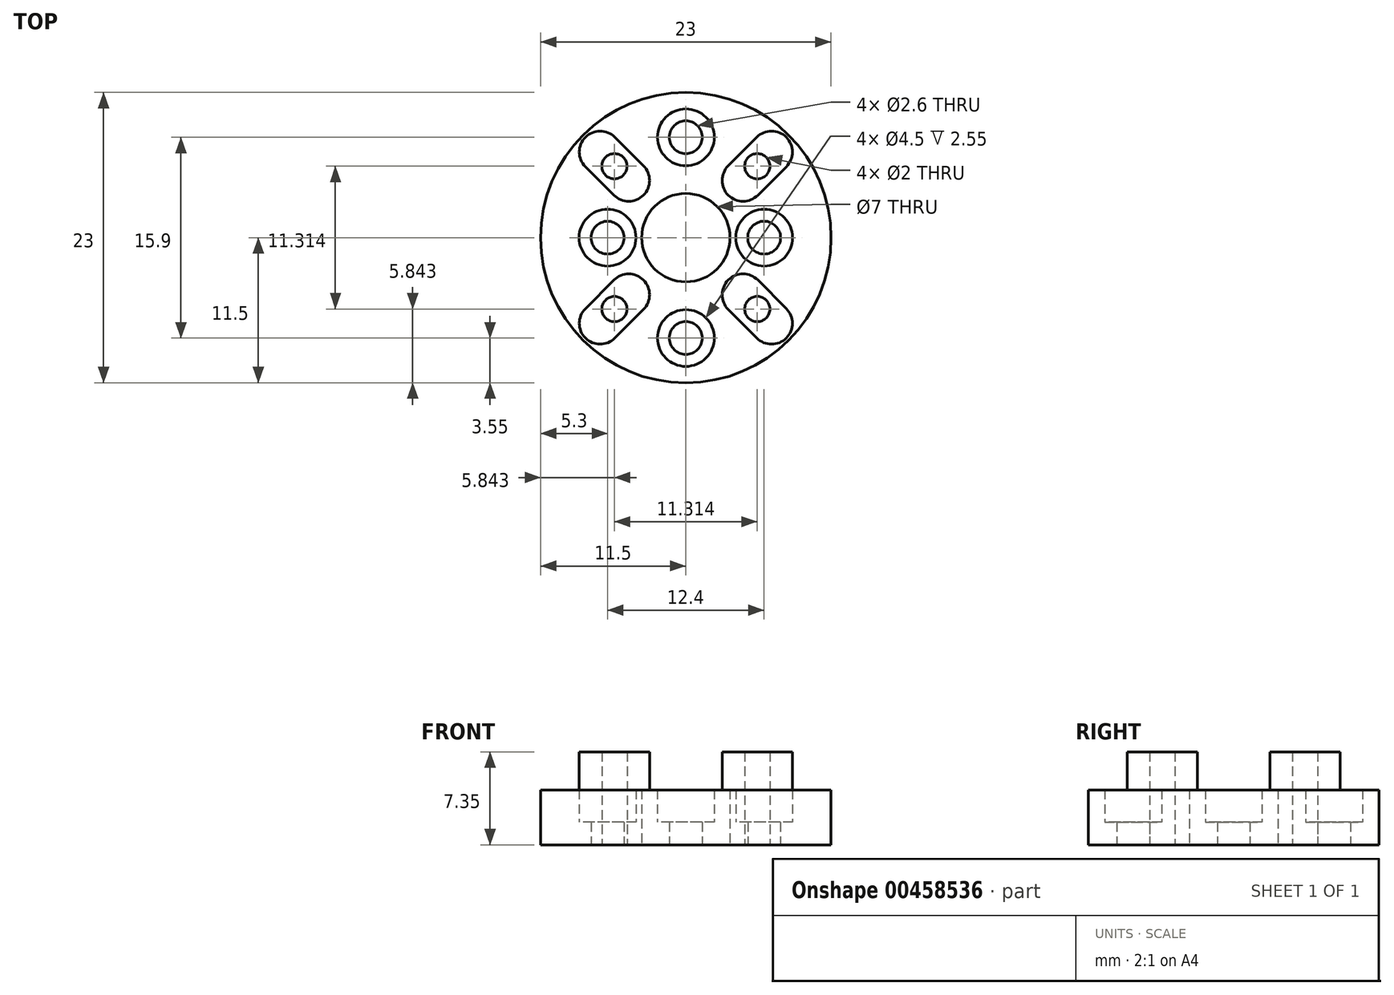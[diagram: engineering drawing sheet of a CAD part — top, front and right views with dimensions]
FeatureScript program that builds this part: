
annotation { "Feature Type Name" : "Feature", "Feature Type Description" : "" }
export const myFeature = defineFeature(function(context is Context, id is Id, definition is map)
    precondition{}
    {
        {
            var Q0;
            Q0=qCreatedBy(makeId("Top.planeOp"),FACE);
            var sketch = newSketch(context, id + "F0", { "sketchPlane" : qUnion([Q0])});
            skCircle(sketch, "E0", {"center": v(0, 0) * mm, "radius": 11.5 * mm});
            skCircle(sketch, "E1", {"center": v(0, 0) * mm, "radius": 3.5 * mm});
            skCircle(sketch, "E2", {"center": v(6.2, 0) * mm, "radius": 1.3 * mm});
            skCircle(sketch, "E3", {"center": v(-6.2, 0) * mm, "radius": 1.3 * mm});
            skCircle(sketch, "E4", {"center": v(0, 7.95) * mm, "radius": 1.3 * mm});
            skCircle(sketch, "E5", {"center": v(0, -7.95) * mm, "radius": 1.3 * mm});
            skSolve(sketch);
        }
        {
            var Q0;
            Q0=qSketchRegion(id+"F0",true);
            extrude(context, id + "F1", {"entities" : qUnion([Q0]), "depth" : 4.35 * mm});
        }
        {
            var Q0;
            Q0=qCreatedBy(makeId("Top.planeOp"),FACE);
            cPlane(context, id + "F2", {"entities" : qUnion([Q0]), "cplaneType" : CPlaneType.OFFSET, "offset" : 4.35 * mm, "width" : 150 * mm, "height" : 150 * mm});
        }
        {
            var Q0;
            Q0=qCreatedBy(id+"F2.planeOp",FACE);
            var sketch = newSketch(context, id + "F3", { "sketchPlane" : qUnion([Q0])});
            skLineSegment(sketch, "E6", {"start": v(0, 0) * mm, "end": v(4.53, -4.53) * mm, "construction": true});
            skLineSegment(sketch, "E7", {"start": v(0, 0) * mm, "end": v(4.53, 4.53) * mm, "construction": true});
            skLineSegment(sketch, "E8", {"start": v(4.53, -4.53) * mm, "end": v(6.79, -6.79) * mm});
            skArc(sketch, "E9.0.startCap", {"start": v(3.36, -5.7) * mm, "mid": v(3.36, -3.36) * mm, "end": v(5.7, -3.36) * mm});
            skArc(sketch, "E9.0.endCap", {"start": v(7.95, -5.62) * mm, "mid": v(7.95, -7.95) * mm, "end": v(5.62, -7.95) * mm});
            skLineSegment(sketch, "E9.0.left", {"start": v(5.7, -3.36) * mm, "end": v(7.95, -5.62) * mm});
            skLineSegment(sketch, "E9.0.right", {"start": v(3.36, -5.7) * mm, "end": v(5.62, -7.95) * mm});
            skLineSegment(sketch, "E10.MirrorCS", {"start": v(4.53, 4.53) * mm, "end": v(6.79, 6.79) * mm});
            skLineSegment(sketch, "E11.MirrorCS", {"start": v(-4.53, 4.53) * mm, "end": v(-6.79, 6.79) * mm});
            skLineSegment(sketch, "E12.MirrorCS", {"start": v(-4.53, -4.53) * mm, "end": v(-6.79, -6.79) * mm});
            skArc(sketch, "E13.0.startCap", {"start": v(5.7, 3.36) * mm, "mid": v(3.36, 3.36) * mm, "end": v(3.36, 5.7) * mm});
            skArc(sketch, "E13.0.endCap", {"start": v(5.62, 7.95) * mm, "mid": v(7.95, 7.95) * mm, "end": v(7.95, 5.62) * mm});
            skLineSegment(sketch, "E13.0.left", {"start": v(3.36, 5.7) * mm, "end": v(5.62, 7.95) * mm});
            skLineSegment(sketch, "E13.0.right", {"start": v(5.7, 3.36) * mm, "end": v(7.95, 5.62) * mm});
            skArc(sketch, "E13.1.startCap", {"start": v(-3.36, 5.7) * mm, "mid": v(-3.36, 3.36) * mm, "end": v(-5.7, 3.36) * mm});
            skArc(sketch, "E13.1.endCap", {"start": v(-7.95, 5.62) * mm, "mid": v(-7.95, 7.95) * mm, "end": v(-5.62, 7.95) * mm});
            skLineSegment(sketch, "E13.1.left", {"start": v(-5.7, 3.36) * mm, "end": v(-7.95, 5.62) * mm});
            skLineSegment(sketch, "E13.1.right", {"start": v(-3.36, 5.7) * mm, "end": v(-5.62, 7.95) * mm});
            skArc(sketch, "E13.2.startCap", {"start": v(-5.7, -3.36) * mm, "mid": v(-3.36, -3.36) * mm, "end": v(-3.36, -5.7) * mm});
            skArc(sketch, "E13.2.endCap", {"start": v(-5.62, -7.95) * mm, "mid": v(-7.95, -7.95) * mm, "end": v(-7.95, -5.62) * mm});
            skLineSegment(sketch, "E13.2.left", {"start": v(-3.36, -5.7) * mm, "end": v(-5.62, -7.95) * mm});
            skLineSegment(sketch, "E13.2.right", {"start": v(-5.7, -3.36) * mm, "end": v(-7.95, -5.62) * mm});
            skSolve(sketch);
        }
        {
            var Q0;
            Q0=qSketchRegion(id+"F3",true);
            extrude(context, id + "F4", {"entities" : qUnion([Q0]), "operationType" : NewBodyOperationType.ADD, "depth" : 3 * mm});
        }
        {
            var Q0;
            Q0=qCreatedBy(makeId("Top.planeOp"),FACE);
            cPlane(context, id + "F5", {"entities" : qUnion([Q0]), "cplaneType" : CPlaneType.OFFSET, "offset" : 1.8 * mm, "width" : 150 * mm, "height" : 150 * mm});
        }
        {
            var Q0;
            Q0=qCreatedBy(id+"F5.planeOp",FACE);
            var sketch = newSketch(context, id + "F6", { "sketchPlane" : qUnion([Q0])});
            skCircle(sketch, "E14", {"center": v(0, -7.95) * mm, "radius": 2.25 * mm});
            skCircle(sketch, "E15", {"center": v(6.2, 0) * mm, "radius": 2.25 * mm});
            skCircle(sketch, "E16", {"center": v(0, 7.95) * mm, "radius": 2.25 * mm});
            skCircle(sketch, "E17", {"center": v(-6.2, 0) * mm, "radius": 2.25 * mm});
            skSolve(sketch);
        }
        {
            var Q0;
            Q0=qSketchRegion(id+"F6",true);
            extrude(context, id + "F7", {"entities" : qUnion([Q0]), "operationType" : NewBodyOperationType.REMOVE, "oppositeDirection" : true, "depth" : -2.6 * mm});
        }
        {
            var Q0;
            Q0=qCreatedBy(makeId("Top.planeOp"),FACE);
            var sketch = newSketch(context, id + "F8", { "sketchPlane" : qUnion([Q0])});
            skCircle(sketch, "E18", {"center": v(5.66, -5.66) * mm, "radius": 1 * mm});
            skCircle(sketch, "E19", {"center": v(5.66, 5.66) * mm, "radius": 1 * mm});
            skCircle(sketch, "E20", {"center": v(-5.66, 5.66) * mm, "radius": 1 * mm});
            skCircle(sketch, "E21", {"center": v(-5.66, -5.66) * mm, "radius": 1 * mm});
            skLineSegment(sketch, "E22", {"start": v(-5.66, 5.66) * mm, "end": v(0, 0) * mm, "construction": true});
            skLineSegment(sketch, "E23", {"start": v(0, 0) * mm, "end": v(-5.66, -5.66) * mm, "construction": true});
            skLineSegment(sketch, "E24", {"start": v(5.66, 5.66) * mm, "end": v(0, 0) * mm, "construction": true});
            skLineSegment(sketch, "E25", {"start": v(5.66, -5.66) * mm, "end": v(0, 0) * mm, "construction": true});
            skSolve(sketch);
        }
        {
            var Q0;
            Q0=qSketchRegion(id+"F8",true);
            extrude(context, id + "F9", {"entities" : qUnion([Q0]), "operationType" : NewBodyOperationType.REMOVE, "depth" : 8 * mm});
        }
    });
